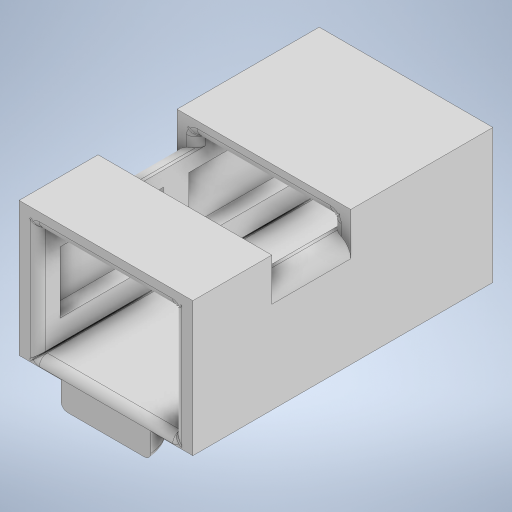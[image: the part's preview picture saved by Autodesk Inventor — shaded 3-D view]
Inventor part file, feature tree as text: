
AUTODESK INVENTOR PART (.ipt)
format: ipt  version: 2023 (Build 270158000, 158)  size: 680,960 bytes
history: native  units: in
note: dims shown in document units (in); Inventor stores cm internally (conversion verified against a paired STEP export)
features: projected_geometry x22, sketch x19, extrude x17, fillet x5
ambient origin geometry x8: Origin, YZ Plane, XZ Plane, XY Plane, X Axis, Y Axis, Z Axis, Center Point
bodies: Solid1 (feature_tree)
feature tree (63):
  extrude  "Extrusion1"  Depth=3.7402in
  extrude  "Extrusion2"  Depth=0.0984in
  extrude  "Extrusion3"  Depth=1.378in
  extrude  "Extrusion4"  Depth=1.7717in
  extrude  "Extrusion5"  Depth=0.2362in TaperAngle=0.0deg
  extrude  "Extrusion6"  Depth=0.9843in TaperAngle=0.0deg
  extrude  "Extrusion7"  Depth=0.0984in TaperAngle=0.0deg
  extrude  "Extrusion9"  Depth=0.0197in
  extrude  "Extrusion11"  Depth=0.0984in
  extrude  "Extrusion12"  Depth=0.6841in
  extrude  "Extrusion15"  TaperAngle=180.0deg  [1 undecoded]
  fillet  "Fillet1"  Radius=0.0197in
  fillet  "Fillet2"  Radius=0.0197in
  fillet  "Fillet3"  Radius=0.1181in
  fillet  "Fillet4"  Radius=0.0197in
  sketch  "Sketch17"  dims[d60=0.3937in d61=0.0in d66=0.3937in d67=0.0in d68=0.1969in]
  sketch  "Sketch18"  dims[d69=0.0984in d70=0.1181in]
  extrude  "Extrusion17"  Depth=0.3937in TaperAngle=0.0deg
  fillet  "Fillet5"  Radius=0.1969in
  extrude  "Extrusion18"  Depth=0.1181in
  extrude  "Extrusion19"  Depth=0.1181in
  extrude  "Extrusion20"  Depth=1.122in
  extrude  "Extrusion21"  Depth=0.0787in
  extrude  "Extrusion22"  Depth=0.6496in
  sketch  "Sketch1"  dims[d0=1.9685in d1=3.7402in]
  sketch  "Sketch2"  dims[d2=1.5748in d3=0.0in d4=0.0984in]
  projected_geometry  "Projected Loop1"
  sketch  "Sketch3"  dims[d5=1.7717in d6=1.378in]
  projected_geometry  "Projected Loop2"
  sketch  "Sketch4"  dims[d7=3.5433in d8=0.0in d9=1.7717in]
  projected_geometry  "Projected Loop3"
  sketch  "Sketch5"  dims[d10=2.7559in d11=0.2362in d12=0.0in]
  projected_geometry  "Projected Loop4"
  sketch  "Sketch6"  dims[d13=0.9843in d14=0.2362in d15=0.0in]
  projected_geometry  "Projected Loop5"
  sketch  "Sketch7"  dims[d16=0.0984in d17=0.0in d18=0.0984in d19=0.0in]
  projected_geometry  "Projected Loop6"
  projected_geometry  "Projected Loop7"
  sketch  "Sketch10"  dims[d20=0.0984in d21=0.0in d29=0.0197in]
  projected_geometry  "Projected Loop9"
  sketch  "Sketch11"  dims[d30=0.0984in d31=0.0in d49=0.8465in]
  projected_geometry  "Projected Loop10"
  sketch  "Sketch12"  dims[d50=0.8268in d51=0.6841in]
  projected_geometry  "Projected Loop11"
  sketch  "Sketch16"  dims[d52=0.3937in d53=0.0in d54=180.0deg d55=0.0197in d56=0.0197in d58=0.1181in d59=0.0197in]
  projected_geometry  "Projected Loop15"
  projected_geometry  "Projected Loop16"
  projected_geometry  "Projected Loop17"
  sketch  "Sketch20"  dims[d71=0.1181in d72=0.0394in]
  projected_geometry  "Projected Loop20"
  projected_geometry  "Projected Loop21"
  projected_geometry  "Projected Loop22"
  sketch  "Sketch21"  dims[d77=1.122in d78=1.122in]
  projected_geometry  "Projected Loop23"
  sketch  "Sketch22"  dims[d79=0.315in d80=0.0in d81=0.0787in]
  projected_geometry  "Projected Loop24"
  sketch  "Sketch23"  dims[d83=0.7677in d84=0.6496in]
  projected_geometry  "Projected Loop25"
  projected_geometry  "Projected Loop26"
  sketch  "Sketch24"  dims[d85=0.1969in]
  projected_geometry  "Projected Loop27"
  sketch  "Sketch25"  dims[d86=0.3543in d87=0.0in d88=1.2894in d89=0.7677in d90=0.2677in d91=0.3074in d92=0.1575in d93=1.2894in d94=0.7677in d95=0.315in d96=0.187in d97=0.0in d98=0.187in d99=0.0in d100=0.7677in d101=1.2894in d102=0.0394in d103=0.7677in d104=1.2894in d105=0.0472in d106=0.0395in d107=0.187in d108=0.0in d109=0.7677in d110=0.6496in d111=0.7677in d112=0.6496in d113=0.0469in d114=0.0394in d115=0.0399in d116=0.187in d117=0.0in]
  projected_geometry  "Projected Loop28"
note: 1 required parameter value undecoded (feature->parameter linkage not recoverable at this tier; creation-order binding heuristic only, values carry confidence <= 0.55)
